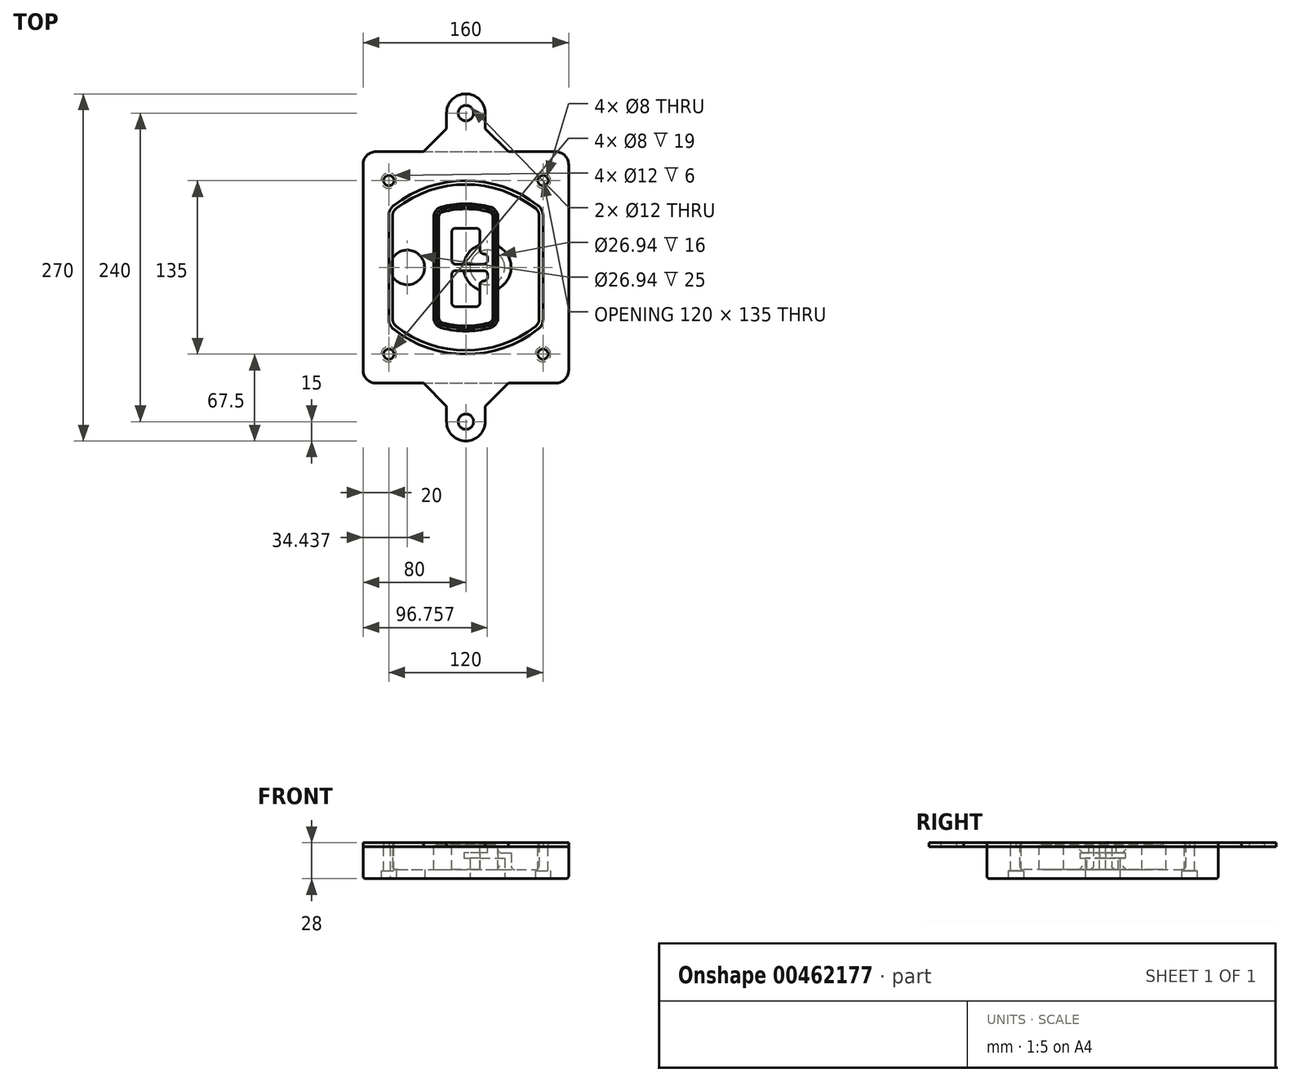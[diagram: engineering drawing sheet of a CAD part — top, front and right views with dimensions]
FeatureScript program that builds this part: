
annotation { "Feature Type Name" : "Feature", "Feature Type Description" : "" }
export const myFeature = defineFeature(function(context is Context, id is Id, definition is map)
    precondition{}
    {
        {
            var Q0;
            Q0=qCreatedBy(makeId("Top.planeOp"),FACE);
            var sketch = newSketch(context, id + "F0", { "sketchPlane" : qUnion([Q0])});
            skPoint(sketch, "E0.rect.middle", {"position": v(0, 0) * mm});
            skLineSegment(sketch, "E1.bottom", {"start": v(-70, -90) * mm, "end": v(70, -90) * mm});
            skLineSegment(sketch, "E1.top", {"start": v(-70, 90) * mm, "end": v(70, 90) * mm});
            skLineSegment(sketch, "E1.left", {"start": v(-80, -80) * mm, "end": v(-80, 80) * mm});
            skLineSegment(sketch, "E1.right", {"start": v(80, -80) * mm, "end": v(80, 80) * mm});
            skLineSegment(sketch, "E2", {"start": v(-80, 90) * mm, "end": v(80, -90) * mm, "construction": true});
            skLineSegment(sketch, "E3", {"start": v(80, 90) * mm, "end": v(-80, -90) * mm, "construction": true});
            skCircle(sketch, "E4", {"center": v(-60, 67.5) * mm, "radius": 4 * mm});
            skCircle(sketch, "E5", {"center": v(60, 67.5) * mm, "radius": 4 * mm});
            skCircle(sketch, "E6", {"center": v(60, -67.5) * mm, "radius": 4 * mm});
            skCircle(sketch, "E7", {"center": v(-60, -67.5) * mm, "radius": 4 * mm});
            skLineSegment(sketch, "E8", {"start": v(-60, 67.5) * mm, "end": v(60, 67.5) * mm, "construction": true});
            skLineSegment(sketch, "E9", {"start": v(60, 67.5) * mm, "end": v(60, -67.5) * mm, "construction": true});
            skLineSegment(sketch, "E10", {"start": v(60, -67.5) * mm, "end": v(-60, -67.5) * mm, "construction": true});
            skLineSegment(sketch, "E11", {"start": v(-60, -67.5) * mm, "end": v(-60, 67.5) * mm, "construction": true});
            skLineSegment(sketch, "E12", {"start": v(-60, 40.3) * mm, "end": v(-60, -40.3) * mm});
            skLineSegment(sketch, "E13", {"start": v(60, 40.3) * mm, "end": v(60, -40.3) * mm});
            skArc(sketch, "E14", {"start": v(56.15, 48.18) * mm, "mid": v(0, 67.5) * mm, "end": v(-56.15, 48.18) * mm});
            skArc(sketch, "E15", {"start": v(-56.15, -48.18) * mm, "mid": v(0, -67.5) * mm, "end": v(56.15, -48.18) * mm});
            skLineSegment(sketch, "E16", {"start": v(-60, 0) * mm, "end": v(60, 0) * mm, "construction": true});
            skPoint(sketch, "E17.visualSharp", {"position": v(-60, -45) * mm});
            skArc(sketch, "E17.filletArc", {"start": v(-60, -40.3) * mm, "mid": v(-58.99, -44.68) * mm, "end": v(-56.15, -48.18) * mm});
            skPoint(sketch, "E18.visualSharp", {"position": v(-60, 45) * mm});
            skArc(sketch, "E18.filletArc", {"start": v(-56.15, 48.18) * mm, "mid": v(-58.99, 44.68) * mm, "end": v(-60, 40.3) * mm});
            skPoint(sketch, "E19.visualSharp", {"position": v(60, 45) * mm});
            skArc(sketch, "E19.filletArc", {"start": v(60, 40.3) * mm, "mid": v(58.99, 44.68) * mm, "end": v(56.15, 48.18) * mm});
            skPoint(sketch, "E20.visualSharp", {"position": v(60, -45) * mm});
            skArc(sketch, "E20.filletArc", {"start": v(56.15, -48.18) * mm, "mid": v(58.99, -44.68) * mm, "end": v(60, -40.3) * mm});
            skPoint(sketch, "E21.visualSharp", {"position": v(-80, 90) * mm});
            skArc(sketch, "E21.filletArc", {"start": v(-70, 90) * mm, "mid": v(-77.07, 87.07) * mm, "end": v(-80, 80) * mm});
            skPoint(sketch, "E22.visualSharp", {"position": v(80, 90) * mm});
            skArc(sketch, "E22.filletArc", {"start": v(80, 80) * mm, "mid": v(77.07, 87.07) * mm, "end": v(70, 90) * mm});
            skPoint(sketch, "E23.visualSharp", {"position": v(80, -90) * mm});
            skArc(sketch, "E23.filletArc", {"start": v(70, -90) * mm, "mid": v(77.07, -87.07) * mm, "end": v(80, -80) * mm});
            skPoint(sketch, "E24.visualSharp", {"position": v(-80, -90) * mm});
            skArc(sketch, "E24.filletArc", {"start": v(-80, -80) * mm, "mid": v(-77.07, -87.07) * mm, "end": v(-70, -90) * mm});
            skArc(sketch, "E25.0", {"start": v(57, 40.3) * mm, "mid": v(56.3, 43.36) * mm, "end": v(54.3, 45.81) * mm});
            skLineSegment(sketch, "E25.1", {"start": v(57, 40.3) * mm, "end": v(57, -40.3) * mm});
            skArc(sketch, "E25.2", {"start": v(54.3, -45.81) * mm, "mid": v(56.3, -43.36) * mm, "end": v(57, -40.3) * mm});
            skArc(sketch, "E25.3", {"start": v(-54.3, -45.81) * mm, "mid": v(0, -64.5) * mm, "end": v(54.3, -45.81) * mm});
            skArc(sketch, "E25.4", {"start": v(-57, -40.3) * mm, "mid": v(-56.3, -43.36) * mm, "end": v(-54.3, -45.81) * mm});
            skArc(sketch, "E25.5", {"start": v(54.3, 45.81) * mm, "mid": v(0, 64.5) * mm, "end": v(-54.3, 45.81) * mm});
            skLineSegment(sketch, "E25.6", {"start": v(-57, 40.3) * mm, "end": v(-57, -40.3) * mm});
            skArc(sketch, "E25.7", {"start": v(-54.3, 45.81) * mm, "mid": v(-56.3, 43.36) * mm, "end": v(-57, 40.3) * mm});
            skArc(sketch, "E26.0", {"start": v(-58.62, 51.33) * mm, "mid": v(-62.58, 46.43) * mm, "end": v(-64, 40.3) * mm});
            skArc(sketch, "E26.1", {"start": v(58.62, 51.33) * mm, "mid": v(0, 71.5) * mm, "end": v(-58.62, 51.33) * mm});
            skArc(sketch, "E26.2", {"start": v(64, 40.3) * mm, "mid": v(62.58, 46.43) * mm, "end": v(58.62, 51.33) * mm});
            skLineSegment(sketch, "E26.3", {"start": v(64, 40.3) * mm, "end": v(64, -40.3) * mm});
            skArc(sketch, "E26.4", {"start": v(58.62, -51.33) * mm, "mid": v(62.58, -46.43) * mm, "end": v(64, -40.3) * mm});
            skLineSegment(sketch, "E26.5", {"start": v(-64, 40.3) * mm, "end": v(-64, -40.3) * mm});
            skArc(sketch, "E26.6", {"start": v(-58.62, -51.33) * mm, "mid": v(0, -71.5) * mm, "end": v(58.62, -51.33) * mm});
            skArc(sketch, "E26.7", {"start": v(-64, -40.3) * mm, "mid": v(-62.58, -46.43) * mm, "end": v(-58.62, -51.33) * mm});
            skSolve(sketch);
        }
        {
            var Q0;
            Q0=makeQuery(id+"F0.imprint","IMPRINT",FACE,{"disambiguationData":[TD([[makeQuery(id+"F0.imprint","IMPRINT",EDGE,{"derivedFrom":sQuery(id+"F0.wireOp",EDGE,"E1.bottom")}),1.0]])]});
            var Q1;
            Q1=makeQuery(id+"F0.imprint","IMPRINT",FACE,{"disambiguationData":[TD([[makeQuery(id+"F0.imprint","IMPRINT",EDGE,{"derivedFrom":sQuery(id+"F0.wireOp",EDGE,"E12")}),1.0]])]});
            var Q2;
            Q2=makeQuery(id+"F0.imprint","IMPRINT",FACE,{"disambiguationData":[TD([[makeQuery(id+"F0.imprint","IMPRINT",EDGE,{"derivedFrom":sQuery(id+"F0.wireOp",EDGE,"E25.0")}),1.0]])]});
            var Q3;
            Q3=makeQuery(id+"F0.imprint","IMPRINT",FACE,{"disambiguationData":[TD([[makeQuery(id+"F0.imprint","IMPRINT",EDGE,{"derivedFrom":sQuery(id+"F0.wireOp",EDGE,"E12")}),-1.0]])]});
            extrude(context, id + "F1", {"entities" : qUnion([Q0, Q1, Q2, Q3]), "oppositeDirection" : true, "depth" : 25 * mm});
        }
        {
            var Q0;
            Q0=makeQuery(id+"F0.imprint","IMPRINT",FACE,{"disambiguationData":[TD([[makeQuery(id+"F0.imprint","IMPRINT",EDGE,{"derivedFrom":sQuery(id+"F0.wireOp",EDGE,"E12")}),1.0]])]});
            extrude(context, id + "F2", {"entities" : qUnion([Q0]), "operationType" : NewBodyOperationType.ADD, "depth" : 3 * mm});
        }
        {
            var Q0;
            Q0=makeQuery(id+"F0.imprint","IMPRINT",FACE,{"disambiguationData":[TD([[makeQuery(id+"F0.imprint","IMPRINT",EDGE,{"derivedFrom":sQuery(id+"F0.wireOp",EDGE,"E25.0")}),1.0]])]});
            extrude(context, id + "F3", {"entities" : qUnion([Q0]), "operationType" : NewBodyOperationType.REMOVE, "oppositeDirection" : true, "depth" : 18 * mm});
        }
        {
            var Q0;
            Q0=makeQuery(id+"F2.opExtrude","CAP_FACE",FACE,{"disambiguationData":[OSD([sQuery(id+"F0.wireOp",EDGE,"E12"),sQuery(id+"F0.wireOp",EDGE,"E13"),sQuery(id+"F0.wireOp",EDGE,"E14"),sQuery(id+"F0.wireOp",EDGE,"E15"),sQuery(id+"F0.wireOp",EDGE,"E17.filletArc"),sQuery(id+"F0.wireOp",EDGE,"E18.filletArc"),sQuery(id+"F0.wireOp",EDGE,"E19.filletArc"),sQuery(id+"F0.wireOp",EDGE,"E20.filletArc"),sQuery(id+"F0.wireOp",EDGE,"E25.0"),sQuery(id+"F0.wireOp",EDGE,"E25.1"),sQuery(id+"F0.wireOp",EDGE,"E25.2"),sQuery(id+"F0.wireOp",EDGE,"E25.3"),sQuery(id+"F0.wireOp",EDGE,"E25.4"),sQuery(id+"F0.wireOp",EDGE,"E25.5"),sQuery(id+"F0.wireOp",EDGE,"E25.6"),sQuery(id+"F0.wireOp",EDGE,"E25.7")])],"isStart":false});
            var sketch = newSketch(context, id + "F4", { "sketchPlane" : qUnion([Q0])});
            skArc(sketch, "E27.0", {"start": v(-19.08, -46.97) * mm, "mid": v(0, -49.5) * mm, "end": v(19.08, -46.97) * mm});
            skArc(sketch, "E28.0", {"start": v(19.08, 46.97) * mm, "mid": v(0, 49.5) * mm, "end": v(-19.08, 46.97) * mm});
            skLineSegment(sketch, "E29", {"start": v(-25, 39.25) * mm, "end": v(-25, -39.25) * mm});
            skLineSegment(sketch, "E30", {"start": v(25, 39.25) * mm, "end": v(25, -39.25) * mm});
            skLineSegment(sketch, "E31", {"start": v(-25, 45.1) * mm, "end": v(25, 45.1) * mm, "construction": true});
            skLineSegment(sketch, "E32", {"start": v(-25, -45.1) * mm, "end": v(25, -45.1) * mm, "construction": true});
            skPoint(sketch, "E33.visualSharp", {"position": v(-25, 45.1) * mm});
            skArc(sketch, "E33.filletArc", {"start": v(-19.08, 46.97) * mm, "mid": v(-23.35, 44.11) * mm, "end": v(-25, 39.25) * mm});
            skPoint(sketch, "E34.visualSharp", {"position": v(25, 45.1) * mm});
            skArc(sketch, "E34.filletArc", {"start": v(25, 39.25) * mm, "mid": v(23.35, 44.11) * mm, "end": v(19.08, 46.97) * mm});
            skPoint(sketch, "E35.visualSharp", {"position": v(25, -45.1) * mm});
            skArc(sketch, "E35.filletArc", {"start": v(19.08, -46.97) * mm, "mid": v(23.35, -44.11) * mm, "end": v(25, -39.25) * mm});
            skPoint(sketch, "E36.visualSharp", {"position": v(-25, -45.1) * mm});
            skArc(sketch, "E36.filletArc", {"start": v(-25, -39.25) * mm, "mid": v(-23.35, -44.11) * mm, "end": v(-19.08, -46.97) * mm});
            skArc(sketch, "E37.0", {"start": v(54.3, 45.81) * mm, "mid": v(0, 64.5) * mm, "end": v(-54.3, 45.81) * mm});
            skArc(sketch, "E37.1", {"start": v(-54.3, 45.81) * mm, "mid": v(-56.3, 43.36) * mm, "end": v(-57, 40.3) * mm});
            skLineSegment(sketch, "E37.2", {"start": v(-57, 40.3) * mm, "end": v(-57, -40.3) * mm});
            skArc(sketch, "E37.3", {"start": v(-57, -40.3) * mm, "mid": v(-56.3, -43.36) * mm, "end": v(-54.3, -45.81) * mm});
            skArc(sketch, "E37.4", {"start": v(-54.3, -45.81) * mm, "mid": v(0, -64.5) * mm, "end": v(54.3, -45.81) * mm});
            skArc(sketch, "E37.5", {"start": v(54.3, -45.81) * mm, "mid": v(56.3, -43.36) * mm, "end": v(57, -40.3) * mm});
            skLineSegment(sketch, "E37.6", {"start": v(57, 40.3) * mm, "end": v(57, -40.3) * mm});
            skArc(sketch, "E37.7", {"start": v(57, 40.3) * mm, "mid": v(56.3, 43.36) * mm, "end": v(54.3, 45.81) * mm});
            skLineSegment(sketch, "E38.0", {"start": v(23, 39.25) * mm, "end": v(23, -39.25) * mm});
            skArc(sketch, "E38.1", {"start": v(18.56, -45.04) * mm, "mid": v(21.76, -42.9) * mm, "end": v(23, -39.25) * mm});
            skArc(sketch, "E38.2", {"start": v(-18.56, -45.04) * mm, "mid": v(0, -47.5) * mm, "end": v(18.56, -45.04) * mm});
            skArc(sketch, "E38.3", {"start": v(-23, -39.25) * mm, "mid": v(-21.76, -42.9) * mm, "end": v(-18.56, -45.04) * mm});
            skLineSegment(sketch, "E38.4", {"start": v(-23, 39.25) * mm, "end": v(-23, -39.25) * mm});
            skArc(sketch, "E38.5", {"start": v(23, 39.25) * mm, "mid": v(21.76, 42.9) * mm, "end": v(18.56, 45.04) * mm});
            skArc(sketch, "E38.6", {"start": v(-18.56, 45.04) * mm, "mid": v(-21.76, 42.9) * mm, "end": v(-23, 39.25) * mm});
            skArc(sketch, "E38.7", {"start": v(18.56, 45.04) * mm, "mid": v(0, 47.5) * mm, "end": v(-18.56, 45.04) * mm});
            skArc(sketch, "E39.0", {"start": v(21, 39.25) * mm, "mid": v(20.18, 41.68) * mm, "end": v(18.04, 43.1) * mm});
            skLineSegment(sketch, "E39.1", {"start": v(21, 39.25) * mm, "end": v(21, -39.25) * mm});
            skArc(sketch, "E39.2", {"start": v(18.04, -43.1) * mm, "mid": v(20.18, -41.68) * mm, "end": v(21, -39.25) * mm});
            skArc(sketch, "E39.3", {"start": v(-18.04, -43.1) * mm, "mid": v(0, -45.5) * mm, "end": v(18.04, -43.1) * mm});
            skArc(sketch, "E39.4", {"start": v(-21, -39.25) * mm, "mid": v(-20.18, -41.68) * mm, "end": v(-18.04, -43.1) * mm});
            skArc(sketch, "E39.5", {"start": v(18.04, 43.1) * mm, "mid": v(0, 45.5) * mm, "end": v(-18.04, 43.1) * mm});
            skLineSegment(sketch, "E39.6", {"start": v(-21, 39.25) * mm, "end": v(-21, -39.25) * mm});
            skArc(sketch, "E39.7", {"start": v(-18.04, 43.1) * mm, "mid": v(-20.18, 41.68) * mm, "end": v(-21, 39.25) * mm});
            skLineSegment(sketch, "E40", {"start": v(-25, 0) * mm, "end": v(25, 0) * mm, "construction": true});
            skLineSegment(sketch, "E41", {"start": v(-11, 5.5) * mm, "end": v(-11, 27.5) * mm});
            skLineSegment(sketch, "E42", {"start": v(-8, 30.5) * mm, "end": v(8, 30.5) * mm});
            skLineSegment(sketch, "E43", {"start": v(11, 27.5) * mm, "end": v(11, 13.5) * mm});
            skLineSegment(sketch, "E44", {"start": v(14, 10.5) * mm, "end": v(14, 10.5) * mm});
            skLineSegment(sketch, "E45", {"start": v(17, 7.5) * mm, "end": v(17, 5.5) * mm});
            skLineSegment(sketch, "E46", {"start": v(14, 2.5) * mm, "end": v(-8, 2.5) * mm});
            skPoint(sketch, "E47.visualSharp", {"position": v(-11, 30.5) * mm});
            skArc(sketch, "E47.filletArc", {"start": v(-8, 30.5) * mm, "mid": v(-10.12, 29.62) * mm, "end": v(-11, 27.5) * mm});
            skPoint(sketch, "E48.visualSharp", {"position": v(11, 30.5) * mm});
            skArc(sketch, "E48.filletArc", {"start": v(11, 27.5) * mm, "mid": v(10.12, 29.62) * mm, "end": v(8, 30.5) * mm});
            skPoint(sketch, "E49.visualSharp", {"position": v(11, 10.5) * mm});
            skArc(sketch, "E49.filletArc", {"start": v(11, 13.5) * mm, "mid": v(11.88, 11.38) * mm, "end": v(14, 10.5) * mm});
            skPoint(sketch, "E50.visualSharp", {"position": v(17, 10.5) * mm});
            skArc(sketch, "E50.filletArc", {"start": v(17, 7.5) * mm, "mid": v(16.12, 9.62) * mm, "end": v(14, 10.5) * mm});
            skPoint(sketch, "E51.visualSharp", {"position": v(17, 2.5) * mm});
            skArc(sketch, "E51.filletArc", {"start": v(14, 2.5) * mm, "mid": v(16.12, 3.38) * mm, "end": v(17, 5.5) * mm});
            skPoint(sketch, "E52.visualSharp", {"position": v(-11, 2.5) * mm});
            skArc(sketch, "E52.filletArc", {"start": v(-11, 5.5) * mm, "mid": v(-10.12, 3.38) * mm, "end": v(-8, 2.5) * mm});
            skLineSegment(sketch, "E53.0.MirrorCS", {"start": v(14, -2.5) * mm, "end": v(-8, -2.5) * mm});
            skArc(sketch, "E54.0.MirrorCS", {"start": v(-11, -5.5) * mm, "mid": v(-10.12, -3.38) * mm, "end": v(-8, -2.5) * mm});
            skLineSegment(sketch, "E55.0.MirrorCS", {"start": v(-11, -5.5) * mm, "end": v(-11, -27.5) * mm});
            skArc(sketch, "E56.0.MirrorCS", {"start": v(-8, -30.5) * mm, "mid": v(-10.12, -29.62) * mm, "end": v(-11, -27.5) * mm});
            skLineSegment(sketch, "E57.0.MirrorCS", {"start": v(-8, -30.5) * mm, "end": v(8, -30.5) * mm});
            skArc(sketch, "E58.0.MirrorCS", {"start": v(11, -27.5) * mm, "mid": v(10.12, -29.62) * mm, "end": v(8, -30.5) * mm});
            skLineSegment(sketch, "E59.0.MirrorCS", {"start": v(11, -27.5) * mm, "end": v(11, -13.5) * mm});
            skArc(sketch, "E60.0.MirrorCS", {"start": v(11, -13.5) * mm, "mid": v(11.88, -11.38) * mm, "end": v(14, -10.5) * mm});
            skArc(sketch, "E61.0.MirrorCS", {"start": v(17, -7.5) * mm, "mid": v(16.12, -9.62) * mm, "end": v(14, -10.5) * mm});
            skLineSegment(sketch, "E62.0.MirrorCS", {"start": v(17, -7.5) * mm, "end": v(17, -5.5) * mm});
            skArc(sketch, "E63.0.MirrorCS", {"start": v(14, -2.5) * mm, "mid": v(16.12, -3.38) * mm, "end": v(17, -5.5) * mm});
            skSolve(sketch);
        }
        {
            var Q0;
            Q0=makeQuery(id+"F4.imprint","IMPRINT",FACE,{"disambiguationData":[TD([[makeQuery(id+"F4.imprint","IMPRINT",EDGE,{"derivedFrom":sQuery(id+"F4.wireOp",EDGE,"E27.0")}),1.0]])]});
            var Q1;
            Q1=makeQuery(id+"F4.imprint","IMPRINT",FACE,{"disambiguationData":[TD([[makeQuery(id+"F4.imprint","IMPRINT",EDGE,{"derivedFrom":sQuery(id+"F4.wireOp",EDGE,"E38.0")}),-1.0]])]});
            var Q2;
            Q2=makeQuery(id+"F4.imprint","IMPRINT",FACE,{"disambiguationData":[TD([[makeQuery(id+"F4.imprint","IMPRINT",EDGE,{"derivedFrom":sQuery(id+"F4.wireOp",EDGE,"E39.0")}),1.0]])]});
            extrude(context, id + "F5", {"entities" : qUnion([Q0, Q1, Q2]), "operationType" : NewBodyOperationType.ADD, "endBound" : BoundingType.UP_TO_NEXT, "oppositeDirection" : true, "depth" : 25 * mm});
        }
        {
            var Q0;
            Q0=makeQuery(id+"F4.imprint","IMPRINT",FACE,{"disambiguationData":[TD([[makeQuery(id+"F4.imprint","IMPRINT",EDGE,{"derivedFrom":sQuery(id+"F4.wireOp",EDGE,"E38.0")}),-1.0]])]});
            extrude(context, id + "F6", {"entities" : qUnion([Q0]), "operationType" : NewBodyOperationType.REMOVE, "oppositeDirection" : true, "depth" : 2 * mm});
        }
        {
            var Q0;
            Q0=makeQuery(id+"F1.opExtrude","CAP_FACE",FACE,{"disambiguationData":[OSD([sQuery(id+"F0.wireOp",EDGE,"E1.bottom"),sQuery(id+"F0.wireOp",EDGE,"E1.top"),sQuery(id+"F0.wireOp",EDGE,"E1.left"),sQuery(id+"F0.wireOp",EDGE,"E1.right"),sQuery(id+"F0.wireOp",EDGE,"E4"),sQuery(id+"F0.wireOp",EDGE,"E5"),sQuery(id+"F0.wireOp",EDGE,"E6"),sQuery(id+"F0.wireOp",EDGE,"E7"),sQuery(id+"F0.wireOp",EDGE,"E21.filletArc"),sQuery(id+"F0.wireOp",EDGE,"E22.filletArc"),sQuery(id+"F0.wireOp",EDGE,"E23.filletArc"),sQuery(id+"F0.wireOp",EDGE,"E24.filletArc")])],"isStart":false});
            var sketch = newSketch(context, id + "F7", { "sketchPlane" : qUnion([Q0])});
            skCircle(sketch, "E64", {"center": v(16.76, 0) * mm, "radius": 13.47 * mm});
            skCircle(sketch, "E65", {"center": v(-45.56, 0) * mm, "radius": 13.47 * mm});
            skLineSegment(sketch, "E66", {"start": v(80, 0) * mm, "end": v(-80, 0) * mm});
            skCircle(sketch, "E67", {"center": v(16.76, 0) * mm, "radius": 18.47 * mm});
            skCircle(sketch, "E68", {"center": v(60, -67.5) * mm, "radius": 6 * mm});
            skCircle(sketch, "E69", {"center": v(-60, -67.5) * mm, "radius": 6 * mm});
            skCircle(sketch, "E70", {"center": v(-60, 67.5) * mm, "radius": 6 * mm});
            skCircle(sketch, "E71", {"center": v(60, 67.5) * mm, "radius": 6 * mm});
            skSolve(sketch);
        }
        {
            var Q0;
            {var subQ1=sQuery(id+"F7.wireOp",EDGE,"E66");var subQ4=sQuery(id+"F7.wireOp",EDGE,"E64");var subQ6=makeQuery(id+"F7.imprint","INTERSECT",VERTEX,{"disambiguationData":[OD(0.0)],"derivedFrom":[subQ4,subQ1]});Q0=makeQuery(id+"F7.imprint","IMPRINT",FACE,{"disambiguationData":[TD([[makeQuery(id+"F7.imprint","IMPRINT",EDGE,{"disambiguationData":[TD([[subQ6,-1.0]])],"derivedFrom":subQ4}),-1.0]])]});}
            var Q1;
            {var subQ0=sQuery(id+"F7.wireOp",EDGE,"E66");var subQ1=sQuery(id+"F7.wireOp",EDGE,"E64");var subQ3=makeQuery(id+"F7.imprint","INTERSECT",VERTEX,{"disambiguationData":[OD(0.0)],"derivedFrom":[subQ1,subQ0]});Q1=makeQuery(id+"F7.imprint","IMPRINT",FACE,{"disambiguationData":[TD([[makeQuery(id+"F7.imprint","IMPRINT",EDGE,{"disambiguationData":[TD([[subQ3,-1.0]])],"derivedFrom":subQ1}),1.0]])]});}
            var Q2;
            {var subQ0=sQuery(id+"F7.wireOp",EDGE,"E66");var subQ1=sQuery(id+"F7.wireOp",EDGE,"E64");var subQ3=makeQuery(id+"F7.imprint","INTERSECT",VERTEX,{"disambiguationData":[OD(0.0)],"derivedFrom":[subQ1,subQ0]});Q2=makeQuery(id+"F7.imprint","IMPRINT",FACE,{"disambiguationData":[TD([[makeQuery(id+"F7.imprint","IMPRINT",EDGE,{"disambiguationData":[TD([[subQ3,1.0]])],"derivedFrom":subQ1}),1.0]])]});}
            var Q3;
            {var subQ1=sQuery(id+"F7.wireOp",EDGE,"E66");var subQ4=sQuery(id+"F7.wireOp",EDGE,"E64");var subQ6=makeQuery(id+"F7.imprint","INTERSECT",VERTEX,{"disambiguationData":[OD(0.0)],"derivedFrom":[subQ4,subQ1]});Q3=makeQuery(id+"F7.imprint","IMPRINT",FACE,{"disambiguationData":[TD([[makeQuery(id+"F7.imprint","IMPRINT",EDGE,{"disambiguationData":[TD([[subQ6,1.0]])],"derivedFrom":subQ4}),-1.0]])]});}
            extrude(context, id + "F8", {"entities" : qUnion([Q0, Q1, Q2, Q3]), "operationType" : NewBodyOperationType.ADD, "oppositeDirection" : true, "depth" : 20 * mm});
        }
        {
            var Q0;
            {var subQ0=sQuery(id+"F7.wireOp",EDGE,"E66");var subQ1=sQuery(id+"F7.wireOp",EDGE,"E64");var subQ3=makeQuery(id+"F7.imprint","INTERSECT",VERTEX,{"disambiguationData":[OD(0.0)],"derivedFrom":[subQ1,subQ0]});Q0=makeQuery(id+"F7.imprint","IMPRINT",FACE,{"disambiguationData":[TD([[makeQuery(id+"F7.imprint","IMPRINT",EDGE,{"disambiguationData":[TD([[subQ3,-1.0]])],"derivedFrom":subQ1}),1.0]])]});}
            var Q1;
            {var subQ0=sQuery(id+"F7.wireOp",EDGE,"E66");var subQ1=sQuery(id+"F7.wireOp",EDGE,"E64");var subQ3=makeQuery(id+"F7.imprint","INTERSECT",VERTEX,{"disambiguationData":[OD(0.0)],"derivedFrom":[subQ1,subQ0]});Q1=makeQuery(id+"F7.imprint","IMPRINT",FACE,{"disambiguationData":[TD([[makeQuery(id+"F7.imprint","IMPRINT",EDGE,{"disambiguationData":[TD([[subQ3,1.0]])],"derivedFrom":subQ1}),1.0]])]});}
            extrude(context, id + "F9", {"entities" : qUnion([Q0, Q1]), "operationType" : NewBodyOperationType.REMOVE, "oppositeDirection" : true, "depth" : 16 * mm});
        }
        {
            var Q0;
            {var subQ0=sQuery(id+"F7.wireOp",EDGE,"E66");var subQ1=sQuery(id+"F7.wireOp",EDGE,"E65");var subQ3=makeQuery(id+"F7.imprint","INTERSECT",VERTEX,{"disambiguationData":[OD(0.0)],"derivedFrom":[subQ1,subQ0]});Q0=makeQuery(id+"F7.imprint","IMPRINT",FACE,{"disambiguationData":[TD([[makeQuery(id+"F7.imprint","IMPRINT",EDGE,{"disambiguationData":[TD([[subQ3,-1.0]])],"derivedFrom":subQ1}),1.0]])]});}
            var Q1;
            {var subQ0=sQuery(id+"F7.wireOp",EDGE,"E66");var subQ1=sQuery(id+"F7.wireOp",EDGE,"E65");var subQ3=makeQuery(id+"F7.imprint","INTERSECT",VERTEX,{"disambiguationData":[OD(0.0)],"derivedFrom":[subQ1,subQ0]});Q1=makeQuery(id+"F7.imprint","IMPRINT",FACE,{"disambiguationData":[TD([[makeQuery(id+"F7.imprint","IMPRINT",EDGE,{"disambiguationData":[TD([[subQ3,1.0]])],"derivedFrom":subQ1}),1.0]])]});}
            extrude(context, id + "F10", {"entities" : qUnion([Q0, Q1]), "operationType" : NewBodyOperationType.REMOVE, "oppositeDirection" : true, "depth" : 25 * mm});
        }
        {
            var Q0;
            Q0=makeQuery(id+"F7.imprint","IMPRINT",FACE,{"disambiguationData":[TD([[makeQuery(id+"F7.imprint","IMPRINT",EDGE,{"derivedFrom":sQuery(id+"F7.wireOp",EDGE,"E68")}),1.0]])]});
            var Q1;
            Q1=makeQuery(id+"F7.imprint","IMPRINT",FACE,{"disambiguationData":[TD([[makeQuery(id+"F7.imprint","IMPRINT",EDGE,{"derivedFrom":makeQuery(id+"F1.opExtrude","CAP_EDGE",EDGE,{"disambiguationData":[OSD([sQuery(id+"F0.wireOp",EDGE,"E5")])],"isStart":false})}),-1.0]])]});
            var Q2;
            Q2=makeQuery(id+"F7.imprint","IMPRINT",FACE,{"disambiguationData":[TD([[makeQuery(id+"F7.imprint","IMPRINT",EDGE,{"derivedFrom":sQuery(id+"F7.wireOp",EDGE,"E69")}),1.0]])]});
            var Q3;
            Q3=makeQuery(id+"F7.imprint","IMPRINT",FACE,{"disambiguationData":[TD([[makeQuery(id+"F7.imprint","IMPRINT",EDGE,{"derivedFrom":makeQuery(id+"F1.opExtrude","CAP_EDGE",EDGE,{"disambiguationData":[OSD([sQuery(id+"F0.wireOp",EDGE,"E4")])],"isStart":false})}),-1.0]])]});
            var Q4;
            Q4=makeQuery(id+"F7.imprint","IMPRINT",FACE,{"disambiguationData":[TD([[makeQuery(id+"F7.imprint","IMPRINT",EDGE,{"derivedFrom":sQuery(id+"F7.wireOp",EDGE,"E70")}),1.0]])]});
            var Q5;
            Q5=makeQuery(id+"F7.imprint","IMPRINT",FACE,{"disambiguationData":[TD([[makeQuery(id+"F7.imprint","IMPRINT",EDGE,{"derivedFrom":makeQuery(id+"F1.opExtrude","CAP_EDGE",EDGE,{"disambiguationData":[OSD([sQuery(id+"F0.wireOp",EDGE,"E7")])],"isStart":false})}),-1.0]])]});
            var Q6;
            Q6=makeQuery(id+"F7.imprint","IMPRINT",FACE,{"disambiguationData":[TD([[makeQuery(id+"F7.imprint","IMPRINT",EDGE,{"derivedFrom":sQuery(id+"F7.wireOp",EDGE,"E71")}),1.0]])]});
            var Q7;
            Q7=makeQuery(id+"F7.imprint","IMPRINT",FACE,{"disambiguationData":[TD([[makeQuery(id+"F7.imprint","IMPRINT",EDGE,{"derivedFrom":makeQuery(id+"F1.opExtrude","CAP_EDGE",EDGE,{"disambiguationData":[OSD([sQuery(id+"F0.wireOp",EDGE,"E6")])],"isStart":false})}),-1.0]])]});
            extrude(context, id + "F11", {"entities" : qUnion([Q0, Q1, Q2, Q3, Q4, Q5, Q6, Q7]), "operationType" : NewBodyOperationType.REMOVE, "oppositeDirection" : true, "depth" : 6 * mm});
        }
        {
            var Q0;
            Q0=makeQuery(id+"F9.boolean.opBoolean","COPY",FACE,{"derivedFrom":makeQuery(id+"F9.opExtrude","CAP_FACE",FACE,{"disambiguationData":[OSD([sQuery(id+"F7.wireOp",EDGE,"E64")])],"isStart":false})});
            var sketch = newSketch(context, id + "F12", { "sketchPlane" : qUnion([Q0])});
            skArc(sketch, "E72.0", {"start": v(11, 17.55) * mm, "mid": v(2.57, 11.82) * mm, "end": v(-1.54, 2.5) * mm});
            skArc(sketch, "E72.1", {"start": v(-1.54, -2.5) * mm, "mid": v(2.57, -11.82) * mm, "end": v(11, -17.55) * mm});
            skLineSegment(sketch, "E73", {"start": v(-1.54, -2.5) * mm, "end": v(14, -2.5) * mm});
            skLineSegment(sketch, "E74.0", {"start": v(14, 2.5) * mm, "end": v(-1.54, 2.5) * mm});
            skArc(sketch, "E74.1", {"start": v(14, 2.5) * mm, "mid": v(16.12, 3.38) * mm, "end": v(17, 5.5) * mm});
            skLineSegment(sketch, "E74.2", {"start": v(17, 7.5) * mm, "end": v(17, 5.5) * mm});
            skArc(sketch, "E74.3", {"start": v(17, 7.5) * mm, "mid": v(16.12, 9.62) * mm, "end": v(14, 10.5) * mm});
            skArc(sketch, "E74.4", {"start": v(11, 13.5) * mm, "mid": v(11.88, 11.38) * mm, "end": v(14, 10.5) * mm});
            skLineSegment(sketch, "E74.5", {"start": v(11, 17.55) * mm, "end": v(11, 13.5) * mm});
            skLineSegment(sketch, "E74.7", {"start": v(14, -2.5) * mm, "end": v(-1.54, -2.5) * mm});
            skArc(sketch, "E74.8", {"start": v(14, -2.5) * mm, "mid": v(16.12, -3.38) * mm, "end": v(17, -5.5) * mm});
            skLineSegment(sketch, "E74.9", {"start": v(17, -7.5) * mm, "end": v(17, -5.5) * mm});
            skArc(sketch, "E74.10", {"start": v(17, -7.5) * mm, "mid": v(16.12, -9.62) * mm, "end": v(14, -10.5) * mm});
            skArc(sketch, "E74.11", {"start": v(11, -13.5) * mm, "mid": v(11.88, -11.38) * mm, "end": v(14, -10.5) * mm});
            skLineSegment(sketch, "E74.12", {"start": v(11, -17.55) * mm, "end": v(11, -13.5) * mm});
            skPoint(sketch, "E75.orphan", {"position": v(11, -27.5) * mm});
            skPoint(sketch, "E76.orphan", {"position": v(-8, -2.5) * mm});
            skPoint(sketch, "E77.orphan", {"position": v(-8, 2.5) * mm});
            skPoint(sketch, "E78.orphan", {"position": v(11, 27.5) * mm});
            skSolve(sketch);
        }
        {
            var Q0;
            {var subQ7=sQuery(id+"F12.wireOp",EDGE,"E72.0");var subQ14=sQuery(id+"F12.wireOp",EDGE,"E72.1");var subQ16=sQuery(id+"F12.wireOp",EDGE,"E74.1");var subQ18=sQuery(id+"F12.wireOp",EDGE,"E74.8");Q0=qUnion([makeQuery(id+"F12.imprint","IMPRINT",FACE,{"disambiguationData":[TD([[makeQuery(id+"F12.imprint","IMPRINT",EDGE,{"derivedFrom":subQ7}),1.0]])]}),makeQuery(id+"F12.imprint","IMPRINT",FACE,{"disambiguationData":[TD([[makeQuery(id+"F12.imprint","IMPRINT",EDGE,{"derivedFrom":subQ14}),1.0]])]}),makeQuery(id+"F12.imprint","IMPRINT",FACE,{"disambiguationData":[TD([[makeQuery(id+"F12.imprint","IMPRINT",EDGE,{"derivedFrom":subQ16}),1.0]])]}),makeQuery(id+"F12.imprint","IMPRINT",FACE,{"disambiguationData":[TD([[makeQuery(id+"F12.imprint","IMPRINT",EDGE,{"derivedFrom":subQ18}),-1.0]])]})]);}
            var Q1;
            Q1=makeQuery(id+"F5.boolean.opBoolean","SPLIT",FACE,{"disambiguationData":[TD([makeQuery(id+"F5.opExtrude","SWEPT_FACE",FACE,{"disambiguationData":[OSD([sQuery(id+"F4.wireOp",EDGE,"E41")])]})])],"derivedFrom":makeQuery(id+"F3.boolean.opBoolean","COPY",FACE,{"derivedFrom":makeQuery(id+"F3.opExtrude","CAP_FACE",FACE,{"disambiguationData":[OSD([sQuery(id+"F0.wireOp",EDGE,"E25.0"),sQuery(id+"F0.wireOp",EDGE,"E25.1"),sQuery(id+"F0.wireOp",EDGE,"E25.2"),sQuery(id+"F0.wireOp",EDGE,"E25.3"),sQuery(id+"F0.wireOp",EDGE,"E25.4"),sQuery(id+"F0.wireOp",EDGE,"E25.5"),sQuery(id+"F0.wireOp",EDGE,"E25.6"),sQuery(id+"F0.wireOp",EDGE,"E25.7")])],"isStart":false})})});
            extrude(context, id + "F13", {"entities" : qUnion([Q0]), "operationType" : NewBodyOperationType.REMOVE, "endBound" : BoundingType.UP_TO_SURFACE, "endBoundEntityFace" : qUnion([Q1]), "depth" : 25 * mm});
        }
        {
            var Q0;
            Q0=makeQuery(id+"F3.boolean.opBoolean","COPY",EDGE,{"derivedFrom":makeQuery(id+"F3.opExtrude","CAP_EDGE",EDGE,{"disambiguationData":[OSD([sQuery(id+"F0.wireOp",EDGE,"E25.6")])],"isStart":false})});
            var Q1;
            Q1=makeQuery(id+"F8.boolean.opBoolean","INTERSECT",EDGE,{"derivedFrom":[makeQuery(id+"F5.opExtrude","SWEPT_FACE",FACE,{"disambiguationData":[OSD([sQuery(id+"F4.wireOp",EDGE,"E30")])]}),makeQuery(id+"F8.opExtrude","CAP_FACE",FACE,{"disambiguationData":[OSD([sQuery(id+"F7.wireOp",EDGE,"E67")])],"isStart":false})]});
            var Q2;
            Q2=makeQuery(id+"F8.boolean.opBoolean","INTERSECT",EDGE,{"disambiguationData":[OD(1.0)],"derivedFrom":[makeQuery(id+"F5.opExtrude","SWEPT_FACE",FACE,{"disambiguationData":[OSD([sQuery(id+"F4.wireOp",EDGE,"E30")])]}),makeQuery(id+"F8.opExtrude","SWEPT_FACE",FACE,{"disambiguationData":[OSD([sQuery(id+"F7.wireOp",EDGE,"E67")])]})]});
            var Q3;
            {var subQ0=sQuery(id+"F4.wireOp",EDGE,"E30");Q3=makeQuery(id+"F8.boolean.opBoolean","SPLIT",EDGE,{"disambiguationData":[TD([makeQuery(id+"F5.opExtrude","SWEPT_FACE",FACE,{"disambiguationData":[OSD([sQuery(id+"F4.wireOp",EDGE,"E35.filletArc")])]})])],"derivedFrom":makeQuery(id+"F5.opExtrude","CAP_EDGE",EDGE,{"disambiguationData":[OSD([subQ0])],"isStart":false})});}
            var Q4;
            {var subQ0=sQuery(id+"F0.wireOp",EDGE,"E25.7");var subQ1=sQuery(id+"F0.wireOp",EDGE,"E25.1");var subQ2=sQuery(id+"F0.wireOp",EDGE,"E25.6");var subQ3=sQuery(id+"F0.wireOp",EDGE,"E25.5");var subQ4=sQuery(id+"F0.wireOp",EDGE,"E25.4");var subQ5=sQuery(id+"F0.wireOp",EDGE,"E25.0");var subQ6=sQuery(id+"F0.wireOp",EDGE,"E25.2");var subQ7=sQuery(id+"F0.wireOp",EDGE,"E25.3");Q4=makeQuery(id+"F8.boolean.opBoolean","INTERSECT",EDGE,{"derivedFrom":[makeQuery(id+"F5.boolean.opBoolean","SPLIT",FACE,{"disambiguationData":[TD([makeQuery(id+"F2.opExtrude","SWEPT_FACE",FACE,{"disambiguationData":[OSD([subQ5])]})])],"derivedFrom":makeQuery(id+"F3.boolean.opBoolean","COPY",FACE,{"derivedFrom":makeQuery(id+"F3.opExtrude","CAP_FACE",FACE,{"disambiguationData":[OSD([subQ5,subQ1,subQ6,subQ7,subQ4,subQ3,subQ2,subQ0])],"isStart":false})})}),makeQuery(id+"F8.opExtrude","SWEPT_FACE",FACE,{"disambiguationData":[OSD([sQuery(id+"F7.wireOp",EDGE,"E67")])]})]});}
            var Q5;
            Q5=makeQuery(id+"F8.boolean.opBoolean","INTERSECT",EDGE,{"disambiguationData":[OD(0.0)],"derivedFrom":[makeQuery(id+"F5.opExtrude","SWEPT_FACE",FACE,{"disambiguationData":[OSD([sQuery(id+"F4.wireOp",EDGE,"E30")])]}),makeQuery(id+"F8.opExtrude","SWEPT_FACE",FACE,{"disambiguationData":[OSD([sQuery(id+"F7.wireOp",EDGE,"E67")])]})]});
            fillet(context, id + "F14", {"entities" : qUnion([Q0, Q1, Q2, Q3, Q4, Q5]), "radius" : 3 * mm, "tangentPropagation" : true, "allowEdgeOverflow" : false});
        }
        {
            var Q0;
            Q0=makeQuery(id+"F1.opExtrude","CAP_EDGE",EDGE,{"disambiguationData":[OSD([sQuery(id+"F0.wireOp",EDGE,"E1.bottom")])],"isStart":false});
            fillet(context, id + "F15", {"entities" : qUnion([Q0]), "radius" : 2 * mm, "tangentPropagation" : true, "allowEdgeOverflow" : false});
        }
        {
            var Q0;
            {var subQ0=sQuery(id+"F0.wireOp",EDGE,"E21.filletArc");var subQ1=sQuery(id+"F0.wireOp",EDGE,"E7");var subQ2=sQuery(id+"F0.wireOp",EDGE,"E6");var subQ3=sQuery(id+"F0.wireOp",EDGE,"E5");var subQ4=sQuery(id+"F0.wireOp",EDGE,"E4");var subQ5=sQuery(id+"F0.wireOp",EDGE,"E22.filletArc");var subQ6=sQuery(id+"F0.wireOp",EDGE,"E1.bottom");var subQ7=sQuery(id+"F0.wireOp",EDGE,"E1.right");var subQ8=sQuery(id+"F0.wireOp",EDGE,"E1.top");var subQ9=sQuery(id+"F0.wireOp",EDGE,"E1.left");var subQ10=sQuery(id+"F0.wireOp",EDGE,"E23.filletArc");var subQ11=sQuery(id+"F0.wireOp",EDGE,"E24.filletArc");Q0=makeQuery(id+"F2.boolean.opBoolean","SPLIT",FACE,{"disambiguationData":[TD([makeQuery(id+"F1.opExtrude","SWEPT_FACE",FACE,{"disambiguationData":[OSD([subQ6])]})])],"derivedFrom":makeQuery(id+"F1.opExtrude","CAP_FACE",FACE,{"disambiguationData":[OSD([subQ6,subQ8,subQ9,subQ7,subQ4,subQ3,subQ2,subQ1,subQ0,subQ5,subQ10,subQ11])],"isStart":true})});}
            var sketch = newSketch(context, id + "F16", { "sketchPlane" : qUnion([Q0])});
            skLineSegment(sketch, "E79.0", {"start": v(-80, -80) * mm, "end": v(-80, 80) * mm});
            skArc(sketch, "E79.1", {"start": v(-70, 90) * mm, "mid": v(-77.07, 87.07) * mm, "end": v(-80, 80) * mm});
            skLineSegment(sketch, "E79.2", {"start": v(-70, 90) * mm, "end": v(70, 90) * mm});
            skArc(sketch, "E79.3", {"start": v(80, 80) * mm, "mid": v(77.07, 87.07) * mm, "end": v(70, 90) * mm});
            skLineSegment(sketch, "E79.4", {"start": v(80, -80) * mm, "end": v(80, 80) * mm});
            skArc(sketch, "E79.5", {"start": v(70, -90) * mm, "mid": v(77.07, -87.07) * mm, "end": v(80, -80) * mm});
            skLineSegment(sketch, "E79.6", {"start": v(-70, -90) * mm, "end": v(70, -90) * mm});
            skArc(sketch, "E79.7", {"start": v(-80, -80) * mm, "mid": v(-77.07, -87.07) * mm, "end": v(-70, -90) * mm});
            skCircle(sketch, "E79.8", {"center": v(-60, -67.5) * mm, "radius": 4 * mm});
            skCircle(sketch, "E79.9", {"center": v(-60, 67.5) * mm, "radius": 4 * mm});
            skCircle(sketch, "E79.10", {"center": v(60, 67.5) * mm, "radius": 4 * mm});
            skCircle(sketch, "E79.11", {"center": v(60, -67.5) * mm, "radius": 4 * mm});
            skArc(sketch, "E79.12", {"start": v(56.15, 48.18) * mm, "mid": v(0, 67.5) * mm, "end": v(-56.15, 48.18) * mm});
            skLineSegment(sketch, "E79.13", {"start": v(60, 40.3) * mm, "end": v(60, -40.3) * mm});
            skArc(sketch, "E79.14", {"start": v(60, 40.3) * mm, "mid": v(58.99, 44.68) * mm, "end": v(56.15, 48.18) * mm});
            skArc(sketch, "E79.15", {"start": v(-56.15, 48.18) * mm, "mid": v(-58.99, 44.68) * mm, "end": v(-60, 40.3) * mm});
            skLineSegment(sketch, "E79.16", {"start": v(-60, 40.3) * mm, "end": v(-60, -40.3) * mm});
            skArc(sketch, "E79.17", {"start": v(-56.15, -48.18) * mm, "mid": v(0, -67.5) * mm, "end": v(56.15, -48.18) * mm});
            skArc(sketch, "E79.18", {"start": v(-60, -40.3) * mm, "mid": v(-58.99, -44.68) * mm, "end": v(-56.15, -48.18) * mm});
            skArc(sketch, "E79.19", {"start": v(56.15, -48.18) * mm, "mid": v(58.99, -44.68) * mm, "end": v(60, -40.3) * mm});
            skCircle(sketch, "E80", {"center": v(0, 120) * mm, "radius": 6 * mm});
            skLineSegment(sketch, "E81", {"start": v(0, 90) * mm, "end": v(0, 120) * mm, "construction": true});
            skArc(sketch, "E82", {"start": v(-15, 120) * mm, "mid": v(0, 135) * mm, "end": v(15, 120) * mm});
            skLineSegment(sketch, "E83", {"start": v(-15, 120) * mm, "end": v(-15, 108) * mm});
            skLineSegment(sketch, "E84", {"start": v(-15, 108) * mm, "end": v(-33, 90) * mm});
            skLineSegment(sketch, "E85.MirrorCS", {"start": v(15, 120) * mm, "end": v(15, 108) * mm});
            skLineSegment(sketch, "E86.MirrorCS", {"start": v(15, 108) * mm, "end": v(33, 90) * mm});
            skLineSegment(sketch, "E87", {"start": v(-80, 0) * mm, "end": v(80, 0) * mm, "construction": true});
            skLineSegment(sketch, "E88.MirrorCS", {"start": v(15, -108) * mm, "end": v(33, -90) * mm});
            skLineSegment(sketch, "E89.MirrorCS", {"start": v(15, -120) * mm, "end": v(15, -108) * mm});
            skArc(sketch, "E90.MirrorCS", {"start": v(-15, -120) * mm, "mid": v(0, -135) * mm, "end": v(15, -120) * mm});
            skLineSegment(sketch, "E91.MirrorCS", {"start": v(-15, -120) * mm, "end": v(-15, -108) * mm});
            skLineSegment(sketch, "E92.MirrorCS", {"start": v(-15, -108) * mm, "end": v(-33, -90) * mm});
            skCircle(sketch, "E93.MirrorC", {"center": v(0, -120) * mm, "radius": 6 * mm});
            skSolve(sketch);
        }
        {
            var Q0;
            Q0=makeQuery(id+"F16.imprint","IMPRINT",FACE,{"disambiguationData":[TD([[makeQuery(id+"F16.imprint","IMPRINT",EDGE,{"derivedFrom":sQuery(id+"F16.wireOp",EDGE,"E80")}),-1.0]])]});
            var Q1;
            Q1=makeQuery(id+"F16.imprint","IMPRINT",FACE,{"disambiguationData":[TD([[makeQuery(id+"F16.imprint","IMPRINT",EDGE,{"derivedFrom":sQuery(id+"F16.wireOp",EDGE,"E79.0")}),-1.0]])]});
            var Q2;
            {var subQ0=sQuery(id+"F16.wireOp",EDGE,"E88.MirrorCS");Q2=makeQuery(id+"F16.imprint","IMPRINT",FACE,{"disambiguationData":[TD([[makeQuery(id+"F16.imprint","IMPRINT",EDGE,{"derivedFrom":subQ0}),1.0]])]});}
            var Q3;
            Q3=makeQuery(id+"F2.opExtrude","CAP_FACE",FACE,{"disambiguationData":[OSD([sQuery(id+"F0.wireOp",EDGE,"E12"),sQuery(id+"F0.wireOp",EDGE,"E13"),sQuery(id+"F0.wireOp",EDGE,"E14"),sQuery(id+"F0.wireOp",EDGE,"E15"),sQuery(id+"F0.wireOp",EDGE,"E17.filletArc"),sQuery(id+"F0.wireOp",EDGE,"E18.filletArc"),sQuery(id+"F0.wireOp",EDGE,"E19.filletArc"),sQuery(id+"F0.wireOp",EDGE,"E20.filletArc"),sQuery(id+"F0.wireOp",EDGE,"E25.0"),sQuery(id+"F0.wireOp",EDGE,"E25.1"),sQuery(id+"F0.wireOp",EDGE,"E25.2"),sQuery(id+"F0.wireOp",EDGE,"E25.3"),sQuery(id+"F0.wireOp",EDGE,"E25.4"),sQuery(id+"F0.wireOp",EDGE,"E25.5"),sQuery(id+"F0.wireOp",EDGE,"E25.6"),sQuery(id+"F0.wireOp",EDGE,"E25.7")])],"isStart":false});
            extrude(context, id + "F17", {"entities" : qUnion([Q0, Q1, Q2]), "endBound" : BoundingType.UP_TO_SURFACE, "endBoundEntityFace" : qUnion([Q3]), "depth" : 25 * mm});
        }
    });
